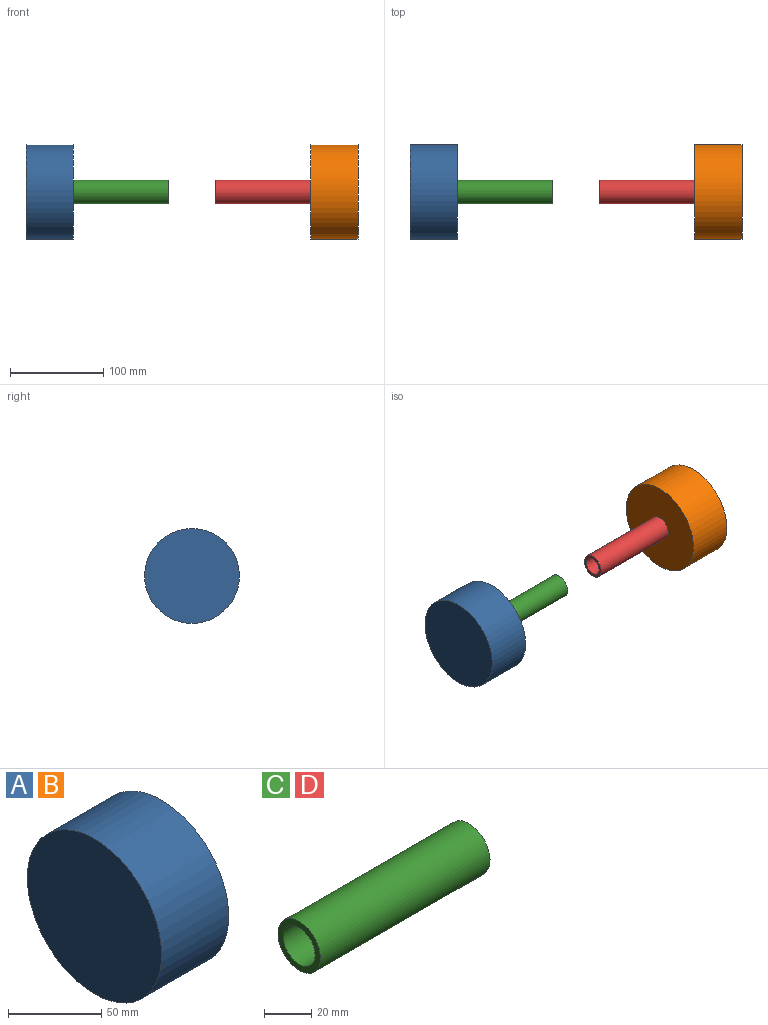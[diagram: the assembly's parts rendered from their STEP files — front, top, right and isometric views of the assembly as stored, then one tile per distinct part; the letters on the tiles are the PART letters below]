
ASSEMBLY  parts=4 mates=3
PART A: 3 faces, bbox 50.8x101.6x101.6 mm
  f0: cylinder r=50.8mm len=101.6mm, axis (-1,0,0), area 16214.6mm2, adj f1,f2
  f1: plane 101.6x101.6mm, normal (1,0,0), area 8107.3mm2, adj f0
  f2: plane 101.6x101.6mm, normal (-1,0,0), area 8107.3mm2, adj f0
PART B: same geometry as A
PART C: 4 faces, bbox 101.6x25.4x25.4 mm
  f0: cylinder r=9.53mm len=101.6mm, axis (-1,0,0), area 6080.5mm2, adj f2,f3
  f1: cylinder r=12.7mm len=101.6mm, axis (-1,0,0), area 8107.3mm2, adj f2,f3
  f2: plane 25.4x25.4mm, normal (1,0,0), area 221.7mm2, adj f0,f1
  f3: plane 25.4x25.4mm, normal (-1,0,0), area 221.7mm2, adj f0,f1
PART D: same geometry as C
PLACE A t=(-59.39,-6.21,20.12)mm
PLACE B t=(245.41,-6.21,20.12)mm
PLACE C t=(-8.59,-6.21,20.12)mm
PLACE D t=(143.81,-6.21,20.12)mm
MATE fastened D.f0 <-> C.f0  axis (-1,0,0) through (143.81,-6.21,20.12)mm
MATE fastened B.f0 <-> D.f1  axis (-1,0,0) through (245.41,-6.21,20.12)mm
MATE fastened C.f1 <-> A.f0  axis (-1,0,0) through (-8.59,-6.21,20.12)mm
